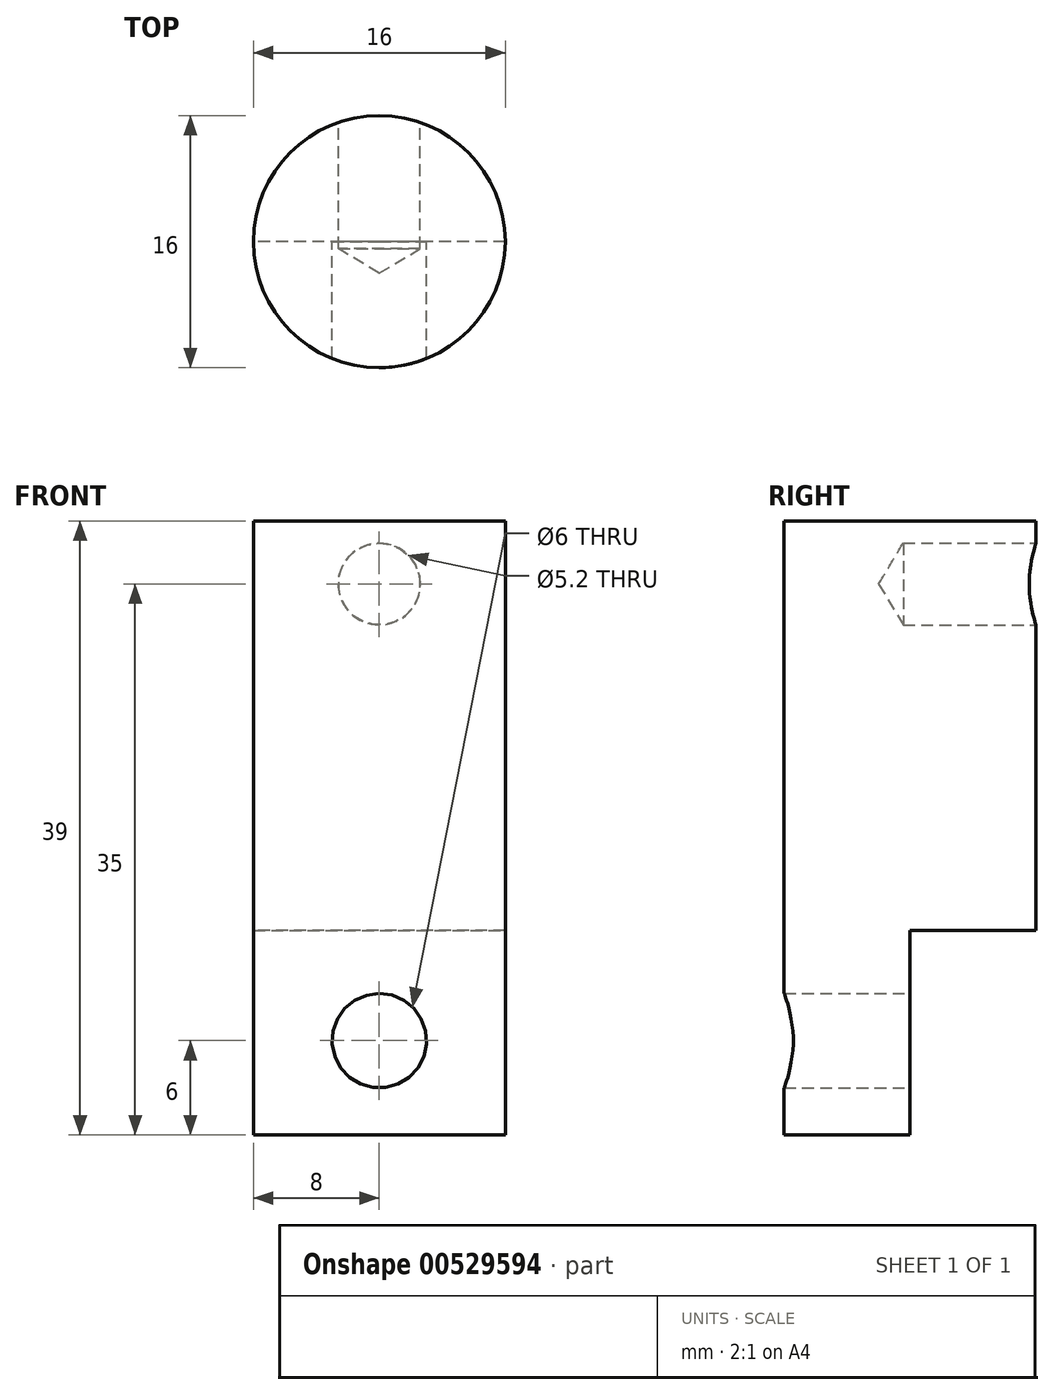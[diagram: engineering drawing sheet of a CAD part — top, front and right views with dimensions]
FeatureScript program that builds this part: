
annotation { "Feature Type Name" : "Feature", "Feature Type Description" : "" }
export const myFeature = defineFeature(function(context is Context, id is Id, definition is map)
    precondition{}
    {
        {
            var Q0;
            Q0=qCreatedBy(makeId("Top.planeOp"),FACE);
            var sketch = newSketch(context, id + "F0", { "sketchPlane" : qUnion([Q0])});
            skCircle(sketch, "E0", {"center": v(0, 0) * mm, "radius": 8 * mm});
            skSolve(sketch);
        }
        {
            var Q0;
            Q0 = qSketchRegion(id + "F0", true);
            extrude(context, id + "F1", {"entities" : qUnion([Q0]), "endBound" : BoundingType.SYMMETRIC, "depth" : 41 * mm, "offsetDistance" : 25 * mm});
        }
        {
            var Q0;
            Q0=makeQuery(id+"F1.opExtrude","CAP_FACE",FACE,{"disambiguationData":[OSD([sQuery(id+"F0.wireOp",EDGE,"E0")])],"isStart":true});
            var sketch = newSketch(context, id + "F2", { "sketchPlane" : qUnion([Q0])});
            skLineSegment(sketch, "E1.bottom", {"start": v(8, 0) * mm, "end": v(-8, 0) * mm});
            skLineSegment(sketch, "E1.top", {"start": v(8, -8) * mm, "end": v(-8, -8) * mm});
            skLineSegment(sketch, "E1.left", {"start": v(8, 0) * mm, "end": v(8, -8) * mm});
            skLineSegment(sketch, "E1.right", {"start": v(-8, 0) * mm, "end": v(-8, -8) * mm});
            skSolve(sketch);
        }
        {
            var Q0;
            Q0 = qSketchRegion(id + "F2", true);
            extrude(context, id + "F3", {"entities" : qUnion([Q0]), "operationType" : NewBodyOperationType.REMOVE, "oppositeDirection" : true, "depth" : 13 * mm, "offsetDistance" : 25 * mm});
        }
        {
            var Q0;
            Q0=makeQuery(id+"F3.boolean.opBoolean","COPY",FACE,{"derivedFrom":makeQuery(id+"F3.opExtrude","SWEPT_FACE",FACE,{"disambiguationData":[OSD([sQuery(id+"F2.wireOp",EDGE,"E1.bottom")])]})});
            var sketch = newSketch(context, id + "F4", { "sketchPlane" : qUnion([Q0])});
            skPoint(sketch, "E2", {"position": v(0, -14.5) * mm});
            skSolve(sketch);
        }
        {
            var Q0;
            Q0=sQuery(id+"F4.wireOp",VERTEX,"E2");
            var Q1;
            Q1=makeQuery(id+"F1.opExtrude","SWEPT_BODY",BODY,{"disambiguationData":[OSD([sQuery(id+"F0.wireOp",EDGE,"E0")])]});
            hole(context, id + "F5", {"style" : HoleStyle.SIMPLE, "endStyle" : HoleEndStyle.THROUGH, "holeDiameter" : 6 * mm, "isTappedThrough" : true, "tappedDepth" : 12 * mm, "tapClearance" : 3, "locations" : qUnion([Q0]), "scope" : qUnion([Q1])});
        }
        {
            var Q0;
            Q0=qCreatedBy(makeId("Front.planeOp"),FACE);
            cPlane(context, id + "F6", {"entities" : qUnion([Q0]), "cplaneType" : CPlaneType.OFFSET, "offset" : 8 * mm, "oppositeDirection" : true, "width" : 150 * mm, "height" : 150 * mm});
        }
        {
            var Q0;
            Q0=qCreatedBy(id+"F6.planeOp",FACE);
            var sketch = newSketch(context, id + "F7", { "sketchPlane" : qUnion([Q0])});
            skPoint(sketch, "E3", {"position": v(0, 14.5) * mm});
            skSolve(sketch);
        }
        {
            var Q0;
            Q0=sQuery(id+"F7.wireOp",VERTEX,"E3");
            var Q1;
            Q1=makeQuery(id+"F1.opExtrude","SWEPT_BODY",BODY,{"disambiguationData":[OSD([sQuery(id+"F0.wireOp",EDGE,"E0")])]});
            hole(context, id + "F8", {"style" : HoleStyle.SIMPLE, "endStyle" : HoleEndStyle.BLIND, "oppositeDirection" : true, "holeDiameter" : 5.2 * mm, "holeDepth" : 8 * mm, "isTappedThrough" : true, "tappedDepth" : 12 * mm, "tapClearance" : 3, "locations" : qUnion([Q0]), "scope" : qUnion([Q1])});
        }
        {
            var Q0;
            Q0=makeQuery(id+"F1.opExtrude","CAP_FACE",FACE,{"disambiguationData":[OSD([sQuery(id+"F0.wireOp",EDGE,"E0")])],"isStart":false});
            var sketch = newSketch(context, id + "F9", { "sketchPlane" : qUnion([Q0])});
            skCircle(sketch, "E4", {"center": v(0, 0) * mm, "radius": 8 * mm});
            skSolve(sketch);
        }
        {
            var Q0;
            Q0 = qSketchRegion(id + "F9", true);
            extrude(context, id + "F10", {"entities" : qUnion([Q0]), "operationType" : NewBodyOperationType.REMOVE, "oppositeDirection" : true, "depth" : 2 * mm, "offsetDistance" : 25 * mm});
        }
    });
